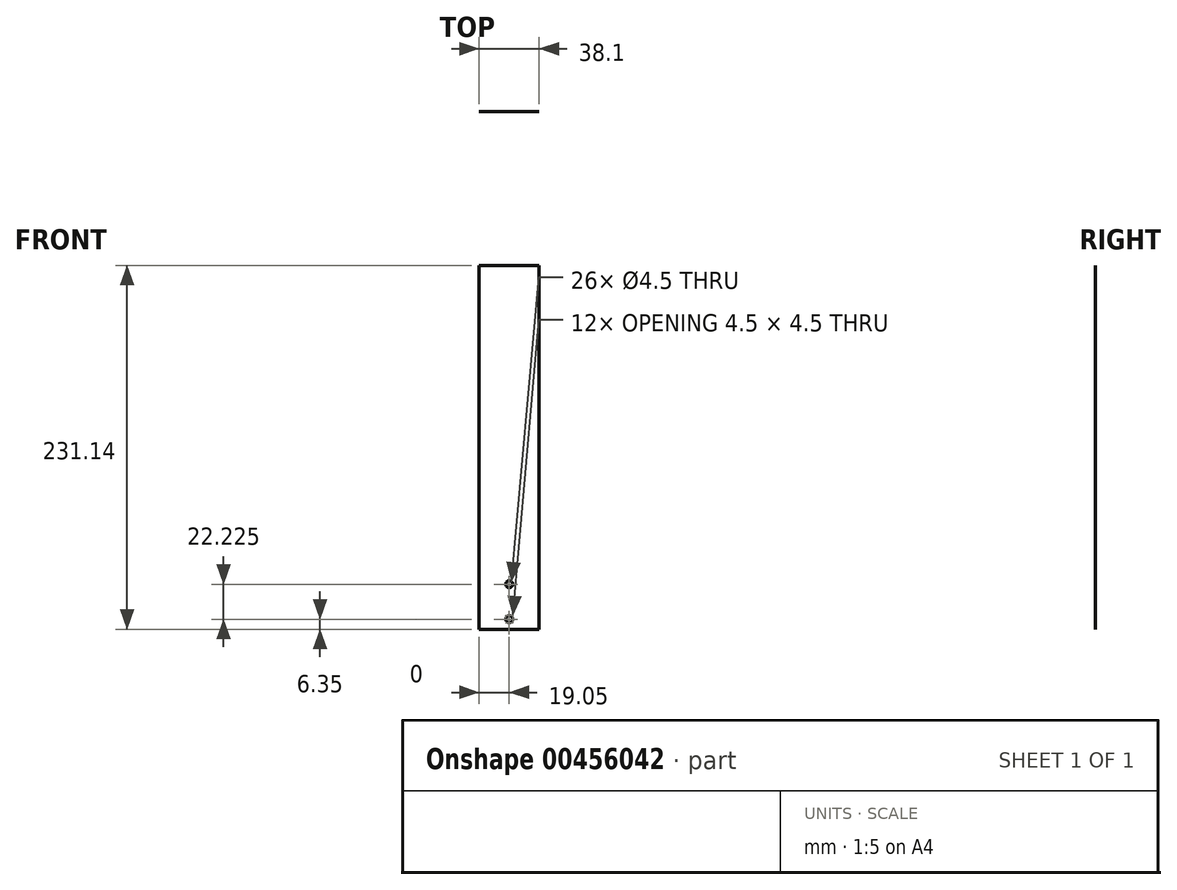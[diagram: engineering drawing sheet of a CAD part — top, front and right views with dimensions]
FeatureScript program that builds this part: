
annotation { "Feature Type Name" : "Feature", "Feature Type Description" : "" }
export const myFeature = defineFeature(function(context is Context, id is Id, definition is map)
    precondition{}
    {
        {
            var Q0;
            Q0=qCreatedBy(makeId("Front.planeOp"),FACE);
            var sketch = newSketch(context, id + "F0", { "sketchPlane" : qUnion([Q0])});
            skLineSegment(sketch, "E0.bottom", {"start": v(0, 0) * mm, "end": v(-38.1, 0) * mm});
            skLineSegment(sketch, "E0.top", {"start": v(0, 231.14) * mm, "end": v(-38.1, 231.14) * mm});
            skLineSegment(sketch, "E0.left", {"start": v(0, 0) * mm, "end": v(0, 231.14) * mm});
            skLineSegment(sketch, "E0.right", {"start": v(-38.1, 0) * mm, "end": v(-38.1, 231.14) * mm});
            skLineSegment(sketch, "E1", {"start": v(-19.05, 231.14) * mm, "end": v(-19.05, 0) * mm, "construction": true});
            skPoint(sketch, "E2", {"position": v(-19.05, 12.7) * mm});
            skPoint(sketch, "E3", {"position": v(-19.05, 57.15) * mm});
            skSolve(sketch);
        }
        {
            var Q0;
            Q0=makeQuery(id+"F0.imprint","IMPRINT",FACE,{"disambiguationData":[TD([[makeQuery(id+"F0.imprint","IMPRINT",EDGE,{"derivedFrom":sQuery(id+"F0.wireOp",EDGE,"E0.bottom")}),-1.0]])]});
            extrude(context, id + "F1", {"entities" : qUnion([Q0]), "depth" : 1 / 203.2 * mm});
        }
        {
            var Q0;
            Q0=makeQuery(id+"F1.opExtrude","CAP_FACE",FACE,{"disambiguationData":[OSD([sQuery(id+"F0.wireOp",EDGE,"E0.bottom"),sQuery(id+"F0.wireOp",EDGE,"E0.top"),sQuery(id+"F0.wireOp",EDGE,"E0.left"),sQuery(id+"F0.wireOp",EDGE,"E0.right")])],"isStart":true});
            var sketch = newSketch(context, id + "F2", { "sketchPlane" : qUnion([Q0])});
            skLineSegment(sketch, "E4", {"start": v(19.05, 231.14) * mm, "end": v(19.05, 0) * mm, "construction": true});
            skPoint(sketch, "E5", {"position": v(19.05, 6.35) * mm});
            skPoint(sketch, "E6", {"position": v(19.05, 28.58) * mm});
            skSolve(sketch);
        }
        {
            var Q0;
            Q0=sQuery(id+"F2.wireOp",VERTEX,"E5");
            var Q1;
            Q1=sQuery(id+"F2.wireOp",VERTEX,"E6");
            var Q2;
            Q2=makeQuery(id+"F1.opExtrude","SWEPT_BODY",BODY,{"disambiguationData":[OSD([sQuery(id+"F0.wireOp",EDGE,"E0.bottom"),sQuery(id+"F0.wireOp",EDGE,"E0.top"),sQuery(id+"F0.wireOp",EDGE,"E0.left"),sQuery(id+"F0.wireOp",EDGE,"E0.right")])]});
            hole(context, id + "F3", {"style" : HoleStyle.SIMPLE, "endStyle" : HoleEndStyle.THROUGH, "standardTappedOrClearance" : lookupTablePath({ "standard" : "ANSI", "fit" : "Normal (ASME)", "size" : "#8", "type" : "Clearance" }), "standardBlindInLast" : lookupTablePath({ "fit" : "Free", "standard" : "ANSI", "size" : "#8", "type" : "Clearance" }), "holeDiameter" : 4.5 * mm, "isTappedThrough" : true, "tappedDepth" : 8.9 * mm, "tapClearance" : 3, "locations" : qUnion([Q0, Q1]), "scope" : qUnion([Q2])});
        }
    });
